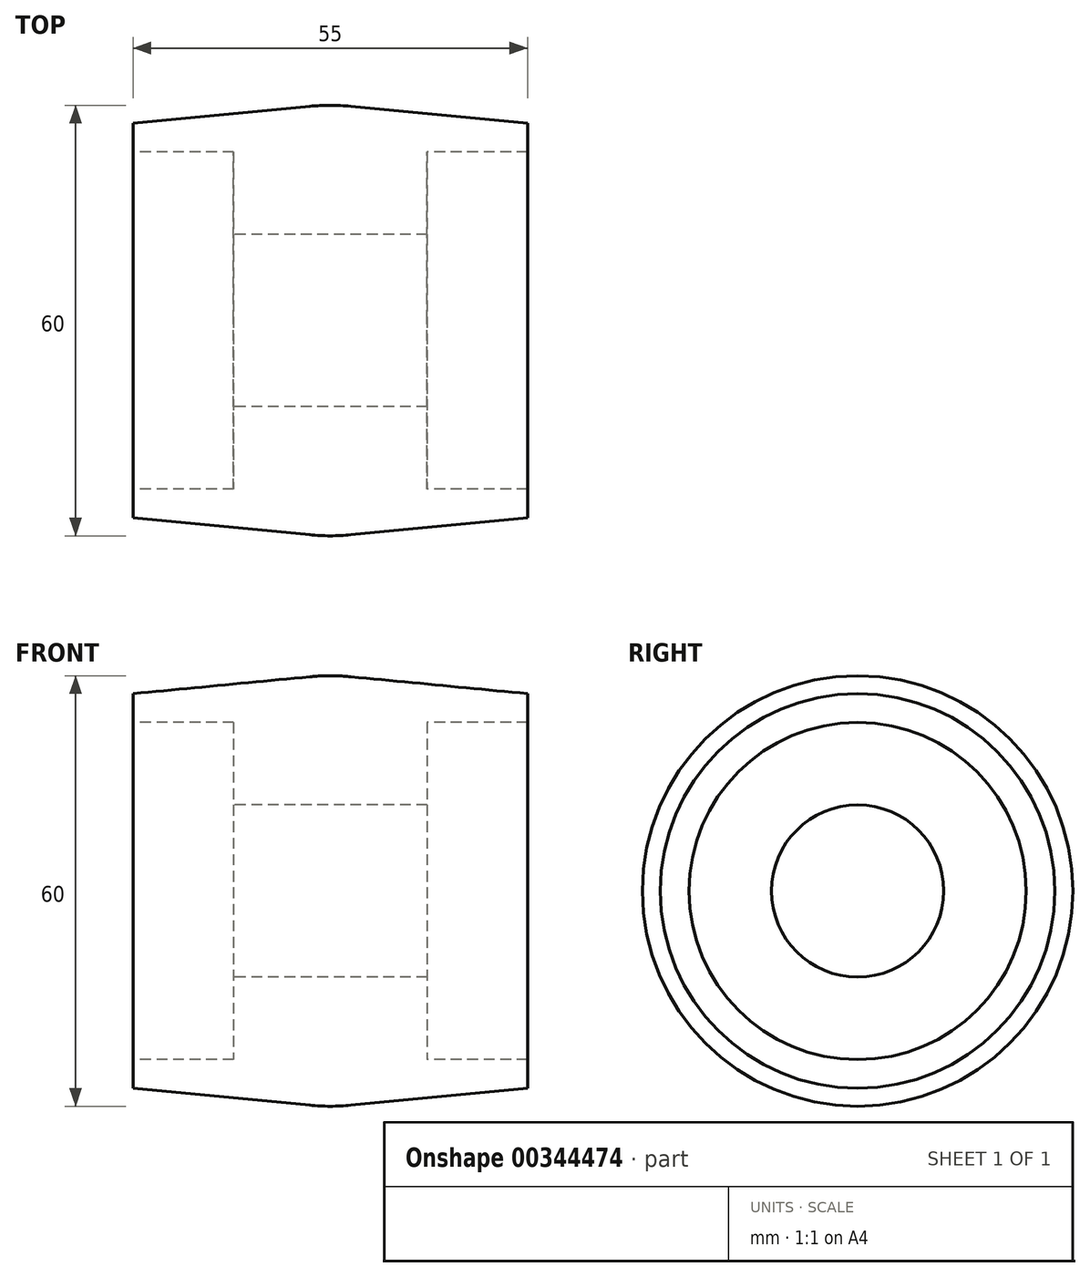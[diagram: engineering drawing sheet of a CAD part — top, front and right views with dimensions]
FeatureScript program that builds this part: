
annotation { "Feature Type Name" : "Feature", "Feature Type Description" : "" }
export const myFeature = defineFeature(function(context is Context, id is Id, definition is map)
    precondition{}
    {
        {
            var Q0;
            Q0=qCreatedBy(makeId("Front.planeOp"),FACE);
            var sketch = newSketch(context, id + "F0", { "sketchPlane" : qUnion([Q0])});
            skLineSegment(sketch, "E0", {"start": v(27.5, 27.5) * mm, "end": v(27.5, 23.5) * mm});
            skLineSegment(sketch, "E1", {"start": v(27.5, 23.5) * mm, "end": v(13.5, 23.5) * mm});
            skLineSegment(sketch, "E2", {"start": v(13.5, 23.5) * mm, "end": v(13.5, 12) * mm});
            skLineSegment(sketch, "E3", {"start": v(13.5, 12) * mm, "end": v(0, 12) * mm});
            skLineSegment(sketch, "E4", {"start": v(0, 12) * mm, "end": v(0, 30) * mm, "construction": true});
            skLineSegment(sketch, "E5", {"start": v(0, 0) * mm, "end": v(27.5, 0) * mm, "construction": true});
            skLineSegment(sketch, "E6", {"start": v(2.86, 29.86) * mm, "end": v(27.5, 27.5) * mm});
            skArc(sketch, "E7", {"start": v(2.86, 29.86) * mm, "mid": v(1.43, 29.97) * mm, "end": v(0, 30) * mm});
            skArc(sketch, "E8.MirrorCS", {"start": v(-2.86, 29.86) * mm, "mid": v(-1.43, 29.97) * mm, "end": v(0, 30) * mm});
            skLineSegment(sketch, "E9.MirrorCS", {"start": v(-13.5, 23.5) * mm, "end": v(-13.5, 12) * mm});
            skLineSegment(sketch, "E10.MirrorCS", {"start": v(-27.5, 27.5) * mm, "end": v(-27.5, 23.5) * mm});
            skLineSegment(sketch, "E11.MirrorCS", {"start": v(-2.86, 29.86) * mm, "end": v(-27.5, 27.5) * mm});
            skLineSegment(sketch, "E12.MirrorCS", {"start": v(-27.5, 23.5) * mm, "end": v(-13.5, 23.5) * mm});
            skLineSegment(sketch, "E13.MirrorCS", {"start": v(-13.5, 12) * mm, "end": v(0, 12) * mm});
            skSolve(sketch);
        }
        {
            var Q0;
            Q0=makeQuery(id+"F0.imprint","IMPRINT",FACE,{"disambiguationData":[TD([[makeQuery(id+"F0.imprint","IMPRINT",EDGE,{"derivedFrom":sQuery(id+"F0.wireOp",EDGE,"E0")}),-1.0]])]});
            var Q1;
            Q1=sQuery(id+"F0.wireOp",EDGE,"E5");
            revolve(context, id + "F1", {"entities" : qUnion([Q0]), "axis" : qUnion([Q1]), "revolveType" : RevolveType.FULL});
        }
    });
